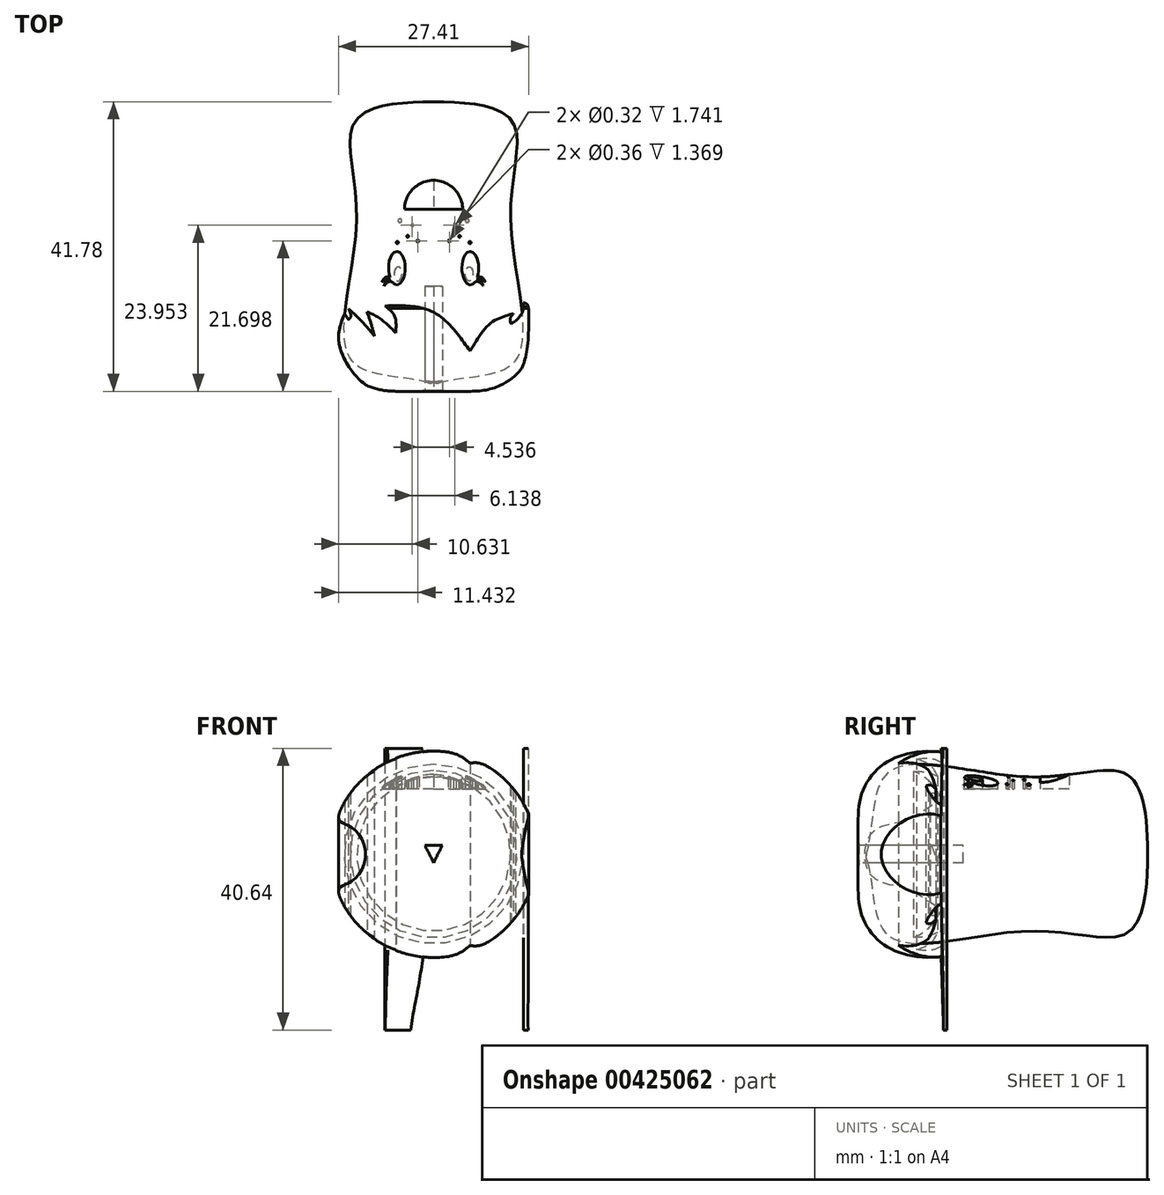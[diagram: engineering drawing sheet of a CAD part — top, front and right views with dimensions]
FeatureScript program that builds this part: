
annotation { "Feature Type Name" : "Feature", "Feature Type Description" : "" }
export const myFeature = defineFeature(function(context is Context, id is Id, definition is map)
    precondition{}
    {
        {
            var Q0;
            Q0=qCreatedBy(makeId("Right.planeOp"),FACE);
            var sketch = newSketch(context, id + "F0", { "sketchPlane" : qUnion([Q0])});
            skFitSpline(sketch, "E0", {"points": [v(44.38, 0) * mm, v(41.22, 11.52) * mm, v(27.41, 11.11) * mm, v(6.97, 11.75) * mm, v(3.55, 0) * mm], "startDerivative": vector(-0.59, 77.15) * mm, "endDerivative": vector(-19.74, -46.77) * mm});
            skLineSegment(sketch, "E1", {"start": v(3.55, 0) * mm, "end": v(44.38, 0) * mm});
            skFitSpline(sketch, "E2", {"points": [v(14.57, 14.72) * mm, v(8.82, 46.12) * mm, v(-16.09, 24.64) * mm, v(0.16, -0.21) * mm], "startDerivative": vector(4.26, 126.12) * mm, "endDerivative": vector(84.77, -69.2) * mm});
            skLineSegment(sketch, "E3", {"start": v(14.57, 14.72) * mm, "end": v(21.9, 12.57) * mm});
            skLineSegment(sketch, "E4", {"start": v(21.9, 12.57) * mm, "end": v(19.43, 45.17) * mm});
            skLineSegment(sketch, "E5", {"start": v(19.43, 45.17) * mm, "end": v(8.82, 46.12) * mm});
            skFitSpline(sketch, "E6", {"points": [v(0.92, -1.47) * mm, v(2.8, 7.55) * mm, v(14.69, 14.7) * mm], "startDerivative": vector(19.78, -1.7) * mm, "endDerivative": vector(33.19, -4.5) * mm});
            skFitSpline(sketch, "E7", {"points": [v(2.59, 0) * mm, v(-10.42, 4.91) * mm, v(-13.93, 13.7) * mm], "startDerivative": vector(-41.56, 0) * mm, "endDerivative": vector(-2.89, 34.67) * mm});
            skPoint(sketch, "E8.startDerivative.orphan", {"position": v(1.4, 4.91) * mm});
            skLineSegment(sketch, "E9", {"start": v(3.01, -0.06) * mm, "end": v(-3.22, -0.06) * mm});
            skLineSegment(sketch, "E10.bottom", {"start": v(2.6, 0.14) * mm, "end": v(-0.97, 0.14) * mm});
            skLineSegment(sketch, "E10.top", {"start": v(2.6, -0.27) * mm, "end": v(-0.97, -0.27) * mm});
            skLineSegment(sketch, "E10.left", {"start": v(2.6, 0.14) * mm, "end": v(2.6, -0.27) * mm});
            skLineSegment(sketch, "E10.right", {"start": v(-0.97, 0.14) * mm, "end": v(-0.97, -0.27) * mm});
            skSolve(sketch);
        }
        {
            var Q0;
            Q0=makeQuery(id+"F0.imprint","IMPRINT",FACE,{"disambiguationData":[TD([[makeQuery(id+"F0.imprint","IMPRINT",EDGE,{"derivedFrom":sQuery(id+"F0.wireOp",EDGE,"E0")}),1.0]])]});
            var Q1;
            Q1=sQuery(id+"F0.wireOp",EDGE,"E1");
            revolve(context, id + "F1", {"entities" : qUnion([Q0]), "axis" : qUnion([Q1]), "revolveType" : RevolveType.FULL});
        }
        {
            var Q0;
            Q0=qCreatedBy(makeId("Top.planeOp"),FACE);
            var sketch = newSketch(context, id + "F2", { "sketchPlane" : qUnion([Q0])});
            skFitSpline(sketch, "E11", {"points": [v(5.37, 8.24) * mm, v(0, 14) * mm, v(-7.02, 14.92) * mm], "startDerivative": vector(-9.44, 13.64) * mm, "endDerivative": vector(-15.4, -0.4) * mm});
            skFitSpline(sketch, "E12", {"points": [v(-7.02, 14.92) * mm, v(-5.65, 13.5) * mm, v(-5.46, 11.04) * mm], "startDerivative": vector(3.5, -2.62) * mm, "endDerivative": vector(-0.32, -5.1) * mm});
            skFitSpline(sketch, "E13", {"points": [v(-5.46, 11.04) * mm, v(-7.83, 13.16) * mm, v(-9.6, 14.06) * mm], "startDerivative": vector(-4.3, 4.28) * mm, "endDerivative": vector(-3.98, 1.66) * mm});
            skFitSpline(sketch, "E14", {"points": [v(-9.6, 14.06) * mm, v(-9.02, 12.36) * mm, v(-8.55, 10.6) * mm], "startDerivative": vector(1.24, -3.4) * mm, "endDerivative": vector(0.88, -3.54) * mm});
            skFitSpline(sketch, "E15", {"points": [v(-8.55, 10.6) * mm, v(-10.36, 12.7) * mm, v(-12.28, 14.51) * mm], "startDerivative": vector(-3.5, 4.26) * mm, "endDerivative": vector(-3.97, 3.57) * mm});
            skFitSpline(sketch, "E16", {"points": [v(-12.28, 14.51) * mm, v(-11.94, 13.45) * mm, v(-12.28, 12.93) * mm], "startDerivative": vector(1, -2.04) * mm, "endDerivative": vector(-1.1, -1.07) * mm});
            skFitSpline(sketch, "E17", {"points": [v(-12.3, 12.97) * mm, v(-12.84, 13.82) * mm], "startDerivative": vector(-0.53, 0.84) * mm, "endDerivative": vector(-0.53, 0.84) * mm});
            skFitSpline(sketch, "E18", {"points": [v(-12.84, 13.82) * mm, v(-13.65, 9.7) * mm, v(-9.6, 3.4) * mm, v(0, 1.44) * mm, v(11.58, 4.24) * mm, v(13.7, 14.51) * mm], "startDerivative": vector(-10.96, -27.13) * mm, "endDerivative": vector(-0.74, 54.3) * mm});
            skFitSpline(sketch, "E19", {"points": [v(13.7, 14.51) * mm, v(13.5, 15.14) * mm, v(12.98, 15.38) * mm], "startDerivative": vector(-0.2, 1.4) * mm, "endDerivative": vector(-1.25, 0.32) * mm});
            skFitSpline(sketch, "E20", {"points": [v(12.98, 15.38) * mm, v(12.82, 14.06) * mm, v(11.81, 12.72) * mm], "startDerivative": vector(0.02, -2.87) * mm, "endDerivative": vector(-2.31, -2.47) * mm});
            skFitSpline(sketch, "E21", {"points": [v(5.25, 8.4) * mm, v(6.63, 10.6) * mm, v(8.47, 12.6) * mm, v(11.52, 13.82) * mm], "startDerivative": vector(4.16, 6.92) * mm, "endDerivative": vector(9.22, 2.69) * mm});
            skFitSpline(sketch, "E22", {"points": [v(11.52, 13.82) * mm, v(11.05, 13.08) * mm, v(11.15, 12.37) * mm], "startDerivative": vector(-1.18, -1.39) * mm, "endDerivative": vector(0.48, -1.51) * mm});
            skFitSpline(sketch, "E23", {"points": [v(11.15, 12.37) * mm, v(11.81, 12.72) * mm], "startDerivative": vector(0.66, 0.35) * mm, "endDerivative": vector(0.66, 0.35) * mm});
            skLineSegment(sketch, "E24", {"start": v(-12.28, 12.93) * mm, "end": v(-12.3, 12.97) * mm});
            skSolve(sketch);
        }
        {
            var Q0;
            {var subQ0=sQuery(id+"F2.wireOp",EDGE,"E12");Q0=makeQuery(id+"F2.imprint","IMPRINT",FACE,{"disambiguationData":[TD([[makeQuery(id+"F2.imprint","IMPRINT",EDGE,{"derivedFrom":subQ0}),1.0]])]});}
            extrude(context, id + "F3", {"entities" : qUnion([Q0]), "depth" : 15.24 * mm, "hasSecondDirection" : true, "secondDirectionOppositeDirection" : true, "secondDirectionDepth" : 25.4 * mm});
        }
        {
            var Q0;
            {var subQ1=sQuery(id+"F0.wireOp",EDGE,"E2");Q0=makeQuery(id+"F0.imprint","IMPRINT",FACE,{"disambiguationData":[TD([[makeQuery(id+"F0.imprint","IMPRINT",EDGE,{"derivedFrom":subQ1}),1.0]])]});}
            var Q1;
            {var subQ0=sQuery(id+"F0.wireOp",EDGE,"E7");var subQ1=sQuery(id+"F0.wireOp",EDGE,"E6");var subQ2=makeQuery(id+"F0.imprint","INTERSECT",VERTEX,{"derivedFrom":[subQ1,subQ0]});Q1=makeQuery(id+"F0.imprint","IMPRINT",FACE,{"disambiguationData":[TD([[makeQuery(id+"F0.imprint","IMPRINT",EDGE,{"disambiguationData":[TD([[subQ2,-1.0]])],"derivedFrom":subQ0}),-1.0]])]});}
            var Q2;
            Q2=sQuery(id+"F0.wireOp",EDGE,"E9");
            revolve(context, id + "F4", {"operationType" : NewBodyOperationType.REMOVE, "entities" : qUnion([Q0, Q1]), "axis" : qUnion([Q2]), "revolveType" : RevolveType.FULL});
        }
        {
            var Q0;
            Q0=qCreatedBy(makeId("Top.planeOp"),FACE);
            var sketch = newSketch(context, id + "F5", { "sketchPlane" : qUnion([Q0])});
            skEllipticalArc(sketch, "E25", {});
            skEllipse(sketch, "E26", {"center": v(-5.13, 19.54) * mm, "majorRadius": 1.03 * mm, "minorRadius": 0.55 * mm, "majorAxis": v(0, 1)});
            skFitSpline(sketch, "E27", {"points": [v(-5.95, 18.36) * mm, v(-6.52, 18.4) * mm, v(-7.16, 17.8) * mm], "startDerivative": vector(-1.29, 0.35) * mm, "endDerivative": vector(-1.12, -1.42) * mm});
            skFitSpline(sketch, "E28", {"points": [v(-7.16, 17.8) * mm, v(-6.8, 18.53) * mm, v(-6.18, 18.75) * mm], "startDerivative": vector(0.52, 1.63) * mm, "endDerivative": vector(1.45, 0.26) * mm});
            skFitSpline(sketch, "E29", {"points": [v(-6.18, 18.75) * mm, v(-7.04, 18.65) * mm, v(-7.43, 18.42) * mm, v(-6.98, 19) * mm, v(-6.29, 19.04) * mm], "startDerivative": vector(-3.15, 0.17) * mm, "endDerivative": vector(2.74, -0.66) * mm});
            skLineSegment(sketch, "E30", {"start": v(0, 28.84) * mm, "end": v(-4.2, 28.84) * mm});
            skArc(sketch, "E31", {"start": v(-4.2, 28.84) * mm, "mid": v(-2.97, 31.8) * mm, "end": v(0, 33.04) * mm});
            skLineSegment(sketch, "E32", {"start": v(0, 33.04) * mm, "end": v(0, 28.84) * mm});
            skCircle(sketch, "E33", {"center": v(-2.27, 24.3) * mm, "radius": 0.16 * mm});
            skCircle(sketch, "E34", {"center": v(-3.74, 24.96) * mm, "radius": 0.14 * mm});
            skCircle(sketch, "E35", {"center": v(-3.07, 26.55) * mm, "radius": 0.18 * mm});
            skCircle(sketch, "E36", {"center": v(-5.24, 24.07) * mm, "radius": 0.17 * mm});
            skCircle(sketch, "E37", {"center": v(-4.85, 27.22) * mm, "radius": 0.26 * mm});
            const initialGuessF5  = {"E25": [-0.00528762536123395, 0.020369630306959152, 0, -1, 0.0024148765951395035, 0.0012020340216499302, 5.6948448982877995, 5.297107771255117]};
            skSetInitialGuess(sketch, initialGuessF5);
            skSolve(sketch);
        }
        {
            var Q0;
            Q0=makeQuery(id+"F5.imprint","IMPRINT",FACE,{"disambiguationData":[TD([[makeQuery(id+"F5.imprint","IMPRINT",EDGE,{"derivedFrom":sQuery(id+"F5.wireOp",EDGE,"E25")}),1.0]])]});
            var Q1;
            Q1=makeQuery(id+"F5.imprint","IMPRINT",FACE,{"disambiguationData":[TD([[makeQuery(id+"F5.imprint","IMPRINT",EDGE,{"derivedFrom":sQuery(id+"F5.wireOp",EDGE,"E30")}),-1.0]])]});
            var Q2;
            Q2=makeQuery(id+"F5.imprint","IMPRINT",FACE,{"disambiguationData":[TD([[makeQuery(id+"F5.imprint","IMPRINT",EDGE,{"derivedFrom":sQuery(id+"F5.wireOp",EDGE,"E35")}),1.0]])]});
            var Q3;
            Q3=makeQuery(id+"F5.imprint","IMPRINT",FACE,{"disambiguationData":[TD([[makeQuery(id+"F5.imprint","IMPRINT",EDGE,{"derivedFrom":sQuery(id+"F5.wireOp",EDGE,"E33")}),1.0]])]});
            var Q4;
            Q4=makeQuery(id+"F5.imprint","IMPRINT",FACE,{"disambiguationData":[TD([[makeQuery(id+"F5.imprint","IMPRINT",EDGE,{"derivedFrom":sQuery(id+"F5.wireOp",EDGE,"E34")}),1.0]])]});
            var Q5;
            Q5=makeQuery(id+"F5.imprint","IMPRINT",FACE,{"disambiguationData":[TD([[makeQuery(id+"F5.imprint","IMPRINT",EDGE,{"derivedFrom":sQuery(id+"F5.wireOp",EDGE,"E37")}),1.0]])]});
            var Q6;
            Q6=makeQuery(id+"F5.imprint","IMPRINT",FACE,{"disambiguationData":[TD([[makeQuery(id+"F5.imprint","IMPRINT",EDGE,{"derivedFrom":sQuery(id+"F5.wireOp",EDGE,"E36")}),1.0]])]});
            extrude(context, id + "F6", {"entities" : qUnion([Q0, Q1, Q2, Q3, Q4, Q5, Q6]), "operationType" : NewBodyOperationType.REMOVE, "depth" : 50.8 * mm, "hasSecondDirection" : true, "secondDirectionOppositeDirection" : false, "secondDirectionDepth" : 9.4 * mm});
        }
        {
            var Q0;
            Q0=makeQuery(id+"F0Fkriingg0lLuM_0.opRevolve","SWEPT_BODY",BODY,{"disambiguationData":[OSD([sQuery(id+"FcjaCqOmTNOoDs9_0.wireOp",EDGE,"IJlq2zB6-M3aP-Jsdj-7luz-pJQfs4NrIwQ5"),sQuery(id+"FcjaCqOmTNOoDs9_0.wireOp",EDGE,"eIos3wdT-DLqv-1gb5-95LA-0mft87HhR8Pk"),sQuery(id+"FcjaCqOmTNOoDs9_0.wireOp",EDGE,"9743d21a-802a-46a4-bee4-47df95381bc2.0"),sQuery(id+"FcjaCqOmTNOoDs9_0.wireOp",EDGE,"37bbe9a4-9c1f-4509-9fdb-9b4277ba79aa")])]});
            var Q1;
            Q1=makeQuery(id+"F1.opRevolve","SWEPT_BODY",BODY,{"disambiguationData":[OSD([sQuery(id+"F0.wireOp",EDGE,"E0"),sQuery(id+"F0.wireOp",EDGE,"E1")])]});
            var Q2;
            Q2=makeQuery(id+"FF2H59dHrTuimo8_0.opLoft","SWEPT_BODY",BODY,{"disambiguationData":[OSD([sQuery(id+"Fna3KxX93nc3Elz_1.wireOp",VERTEX,"b8674463-fdf9-4ea2-bcef-a59d08cb3e68.end"),makeQuery(id+"FEjDWbCm1XSL3kP_1.imprint","IMPRINT",FACE,{"disambiguationData":[TD([[makeQuery(id+"FEjDWbCm1XSL3kP_1.imprint","IMPRINT",EDGE,{"derivedFrom":sQuery(id+"FEjDWbCm1XSL3kP_1.wireOp",EDGE,"qi9NbX7A-QAR4-lWQU-mpFh-FFtPoWwB5aRG")}),1.0]])]}),sQuery(id+"Fv3SpyofjgzSIEd_1.wireOp",EDGE,"8EvIdRlJ-bgR2-O6sq-8ksY-BayLv84Unow1"),sQuery(id+"FXCYf9dFtplMc20_1.wireOp",EDGE,"75vGpwPq-zarO-ital-3VJf-SL7g84x6zOEV"),sQuery(id+"FTaAUjKW1lkMqOU_1.wireOp",EDGE,"2HbUxe87-BOtM-Uitn-LHyD-O426OYk3ySaA"),sQuery(id+"F8P8EEW9tqeLBEy_1.wireOp",EDGE,"CFNe4ozF-EejB-gLrr-czKh-FrGxCwPqhpyT"),sQuery(id+"FEaHKjIRaeH20SI_1.wireOp",EDGE,"NIflC6qb-iB86-vJC8-sYbj-FDsNLH7QAThX"),sQuery(id+"FAITrqFxkk7kzFb_1.wireOp",EDGE,"UlK8HozW-vKKD-JPoU-sZjp-tT1CQpu8iE3o")])]});
            var Q3;
            Q3=qCreatedBy(makeId("Right.planeOp"),FACE);
            mirror(context, id + "F7", {"entities" : qUnion([Q0, Q1, Q2]), "mirrorPlane" : qUnion([Q3])});
        }
        {
            var Q0;
            {var subQ3=sQuery(id+"F0.wireOp",EDGE,"E7");var subQ9=sQuery(id+"F0.wireOp",EDGE,"E6");var subQ10=makeQuery(id+"F0.imprint","INTERSECT",VERTEX,{"derivedFrom":[subQ9,subQ3]});Q0=makeQuery(id+"F0.imprint","IMPRINT",FACE,{"disambiguationData":[TD([[makeQuery(id+"F0.imprint","IMPRINT",EDGE,{"disambiguationData":[TD([[subQ10,-1.0]])],"derivedFrom":subQ3}),1.0]])]});}
            var Q1;
            {var subQ5=sQuery(id+"F0.wireOp",EDGE,"E10.top");Q1=makeQuery(id+"F0.imprint","IMPRINT",FACE,{"disambiguationData":[TD([[makeQuery(id+"F0.imprint","IMPRINT",EDGE,{"derivedFrom":subQ5}),-1.0]])]});}
            extrude(context, id + "F8", {"entities" : qUnion([Q0, Q1]), "operationType" : NewBodyOperationType.REMOVE, "endBound" : BoundingType.SYMMETRIC, "oppositeDirection" : true, "depth" : 0.5 * mm, "hasSecondDirection" : true, "secondDirectionBound" : SecondDirectionBoundingType.THROUGH_ALL, "secondDirectionOppositeDirection" : false, "secondDirectionDepth" : 25.4 * mm});
        }
        {
            var Q0;
            Q0=qCreatedBy(makeId("Front.planeOp"),FACE);
            var sketch = newSketch(context, id + "F9", { "sketchPlane" : qUnion([Q0])});
            skLineSegment(sketch, "E38", {"start": v(-1.27, 1.27) * mm, "end": v(1.27, 1.27) * mm});
            skLineSegment(sketch, "E39", {"start": v(1.27, 1.27) * mm, "end": v(0, -1.27) * mm});
            skLineSegment(sketch, "E40", {"start": v(0, -1.27) * mm, "end": v(-1.27, 1.27) * mm});
            skSolve(sketch);
        }
        {
            var Q0;
            Q0=makeQuery(id+"F9.imprint","IMPRINT",FACE,{"disambiguationData":[TD([[makeQuery(id+"F9.imprint","IMPRINT",EDGE,{"derivedFrom":sQuery(id+"F9.wireOp",EDGE,"E38")}),-1.0]])]});
            extrude(context, id + "F10", {"entities" : qUnion([Q0]), "operationType" : NewBodyOperationType.REMOVE, "oppositeDirection" : true, "depth" : 17.78 * mm});
        }
    });
